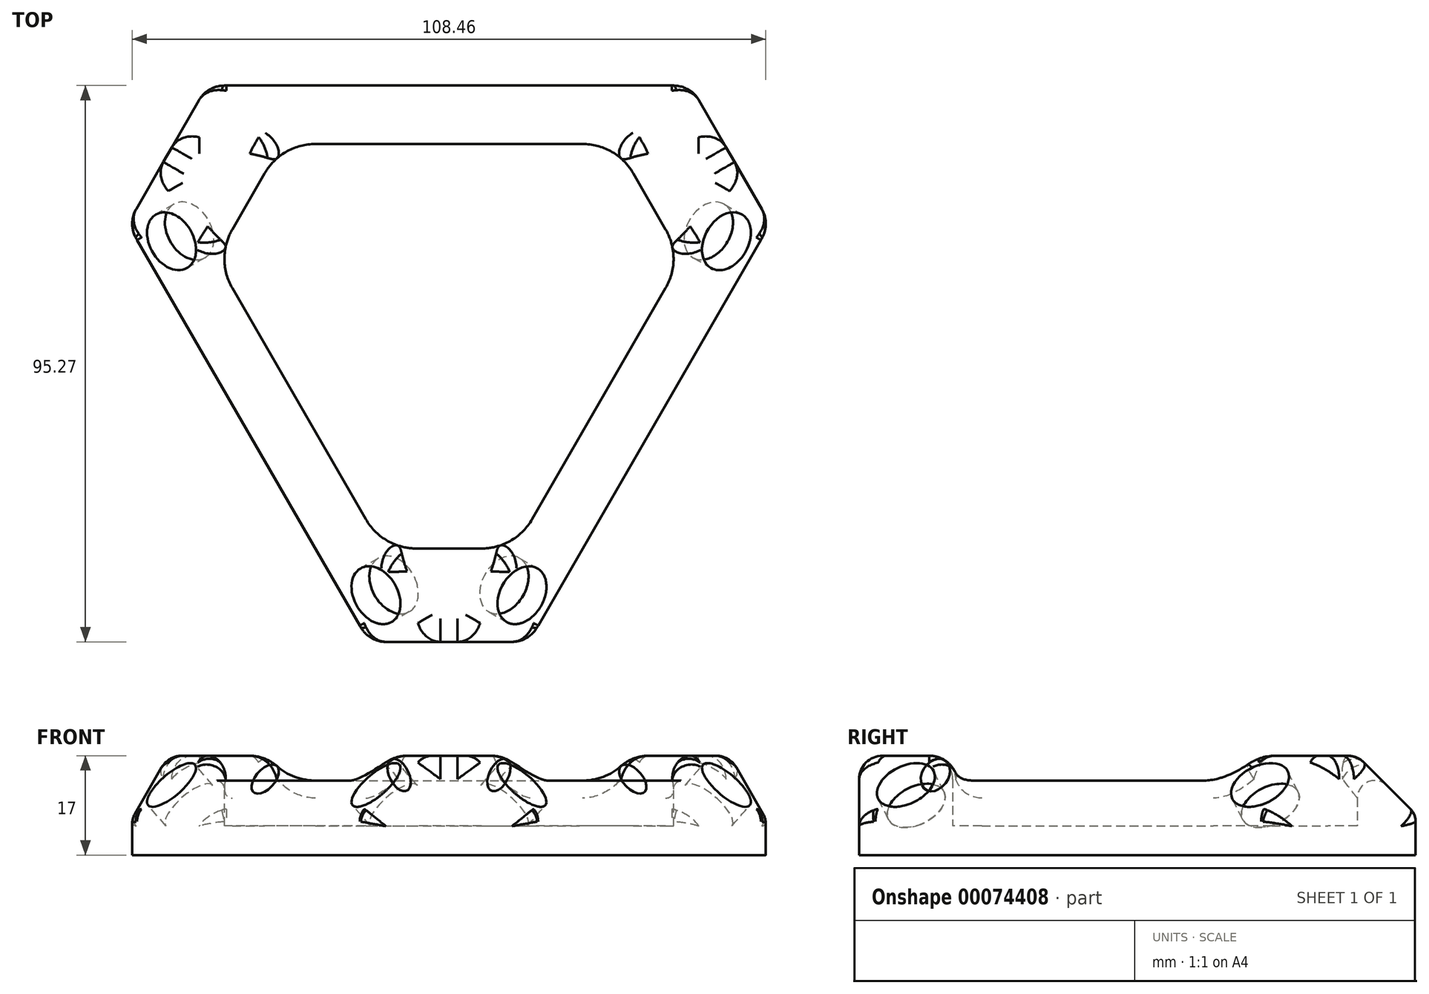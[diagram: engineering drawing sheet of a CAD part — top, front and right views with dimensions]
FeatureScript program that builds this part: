
annotation { "Feature Type Name" : "Feature", "Feature Type Description" : "" }
export const myFeature = defineFeature(function(context is Context, id is Id, definition is map)
    precondition{}
    {
        {
            var Q0;
            Q0=qCreatedBy(makeId("Top.planeOp"),FACE);
            var sketch = newSketch(context, id + "F0", { "sketchPlane" : qUnion([Q0])});
            skCircle(sketch, "E0.cCircle", {"center": v(0, 0) * mm, "radius": 34.64 * mm, "construction": true});
            skLineSegment(sketch, "E0.0", {"start": v(-60, 34.64) * mm, "end": v(60, 34.64) * mm, "construction": true});
            skLineSegment(sketch, "E0.1", {"start": v(60, 34.64) * mm, "end": v(0, -69.28) * mm, "construction": true});
            skLineSegment(sketch, "E0.2", {"start": v(0, -69.28) * mm, "end": v(-60, 34.64) * mm, "construction": true});
            skPoint(sketch, "E0.0.midPoint", {"position": v(0, 34.64) * mm});
            skCircle(sketch, "E1.cCircle", {"center": v(0, 0) * mm, "radius": 60.62 * mm, "construction": true});
            skLineSegment(sketch, "E1.0", {"start": v(-35, 60.62) * mm, "end": v(35, 60.62) * mm, "construction": true});
            skLineSegment(sketch, "E1.1", {"start": v(35, 60.62) * mm, "end": v(70, 0) * mm, "construction": true});
            skLineSegment(sketch, "E1.2", {"start": v(70, 0) * mm, "end": v(35, -60.62) * mm, "construction": true});
            skLineSegment(sketch, "E1.3", {"start": v(35, -60.62) * mm, "end": v(-35, -60.62) * mm, "construction": true});
            skLineSegment(sketch, "E1.4", {"start": v(-35, -60.62) * mm, "end": v(-70, 0) * mm, "construction": true});
            skLineSegment(sketch, "E1.5", {"start": v(-70, 0) * mm, "end": v(-35, 60.62) * mm, "construction": true});
            skPoint(sketch, "E1.0.midPoint", {"position": v(0, 60.62) * mm});
            skLineSegment(sketch, "E2", {"start": v(-35, 60.62) * mm, "end": v(-35, -60.62) * mm, "construction": true});
            skLineSegment(sketch, "E3", {"start": v(35, 60.62) * mm, "end": v(35, -60.62) * mm, "construction": true});
            skLineSegment(sketch, "E4", {"start": v(-70, 0) * mm, "end": v(35, 60.62) * mm, "construction": true});
            skLineSegment(sketch, "E5", {"start": v(-35, -60.62) * mm, "end": v(70, 0) * mm, "construction": true});
            skLineSegment(sketch, "E6", {"start": v(70, 0) * mm, "end": v(-35, 60.62) * mm, "construction": true});
            skLineSegment(sketch, "E7", {"start": v(35, -60.62) * mm, "end": v(-70, 0) * mm, "construction": true});
            skLineSegment(sketch, "E8", {"start": v(-35, 34.64) * mm, "end": v(35, 34.64) * mm, "construction": true});
            skLineSegment(sketch, "E9", {"start": v(35, 34.64) * mm, "end": v(47.5, 13) * mm, "construction": true});
            skLineSegment(sketch, "E10", {"start": v(-35, 34.64) * mm, "end": v(-47.5, 13) * mm, "construction": true});
            skLineSegment(sketch, "E11", {"start": v(-47.5, 13) * mm, "end": v(-12.5, -47.63) * mm, "construction": true});
            skLineSegment(sketch, "E12", {"start": v(-12.5, -47.63) * mm, "end": v(12.5, -47.63) * mm, "construction": true});
            skLineSegment(sketch, "E13", {"start": v(12.5, -47.63) * mm, "end": v(47.5, 13) * mm, "construction": true});
            skLineSegment(sketch, "E14", {"start": v(-28.65, 29.64) * mm, "end": v(28.65, 29.64) * mm});
            skLineSegment(sketch, "E15", {"start": v(28.65, 29.64) * mm, "end": v(40, 10) * mm});
            skLineSegment(sketch, "E16", {"start": v(40, 10) * mm, "end": v(11.35, -39.63) * mm});
            skLineSegment(sketch, "E17", {"start": v(11.35, -39.63) * mm, "end": v(-11.35, -39.63) * mm});
            skLineSegment(sketch, "E18", {"start": v(-11.35, -39.63) * mm, "end": v(-40, 10) * mm});
            skLineSegment(sketch, "E19", {"start": v(-40, 10) * mm, "end": v(-28.65, 29.64) * mm});
            skLineSegment(sketch, "E20", {"start": v(-41.35, 39.64) * mm, "end": v(41.35, 39.64) * mm});
            skLineSegment(sketch, "E21", {"start": v(41.35, 39.64) * mm, "end": v(55, 16) * mm});
            skLineSegment(sketch, "E22", {"start": v(55, 16) * mm, "end": v(13.65, -55.63) * mm});
            skLineSegment(sketch, "E23", {"start": v(13.65, -55.63) * mm, "end": v(-13.65, -55.63) * mm});
            skLineSegment(sketch, "E24", {"start": v(-13.65, -55.63) * mm, "end": v(-55, 16) * mm});
            skLineSegment(sketch, "E25", {"start": v(-55, 16) * mm, "end": v(-41.35, 39.64) * mm});
            skSolve(sketch);
        }
        {
            var Q0;
            Q0=makeQuery(id+"F0.imprint","IMPRINT",FACE,{"disambiguationData":[TD([[makeQuery(id+"F0.imprint","IMPRINT",EDGE,{"derivedFrom":sQuery(id+"F0.wireOp",EDGE,"E14")}),-1.0]])]});
            extrude(context, id + "F1", {"entities" : qUnion([Q0]), "depth" : 5 * mm});
        }
        {
            var Q0;
            Q0 = qSketchRegion(id + "F0", true);
            extrude(context, id + "F2", {"entities" : qUnion([Q0]), "operationType" : NewBodyOperationType.ADD, "depth" : 17 * mm});
        }
        {
            var Q0;
            Q0=makeQuery(id+"F2.opExtrude","CAP_EDGE",EDGE,{"disambiguationData":[OSD([sQuery(id+"F0.wireOp",EDGE,"E24")])],"isStart":false});
            var Q1;
            Q1=makeQuery(id+"F2.opExtrude","CAP_EDGE",EDGE,{"disambiguationData":[OSD([sQuery(id+"F0.wireOp",EDGE,"E22")])],"isStart":false});
            var Q2;
            Q2=makeQuery(id+"F2.opExtrude","CAP_EDGE",EDGE,{"disambiguationData":[OSD([sQuery(id+"F0.wireOp",EDGE,"E20")])],"isStart":false});
            chamfer(context, id + "F3", {"entities" : qUnion([Q0, Q1, Q2]), "width" : 10 * mm, "tangentPropagation" : true});
        }
        {
            var Q0;
            Q0=makeQuery(id+"F3.opChamfer","BLEND_FACE",FACE,{"disambiguationData":[OSD([sQuery(id+"F0.wireOp",EDGE,"E24")])]});
            var sketch = newSketch(context, id + "F4", { "sketchPlane" : qUnion([Q0])});
            skLineSegment(sketch, "E26", {"start": v(-40.38, 24.14) * mm, "end": v(15.58, -44.4) * mm, "construction": true});
            skLineSegment(sketch, "E27", {"start": v(-12.4, -10.13) * mm, "end": v(9.73, -37.24) * mm, "construction": true});
            skLineSegment(sketch, "E28", {"start": v(-12.4, -10.13) * mm, "end": v(-34.54, 16.99) * mm, "construction": true});
            skCircle(sketch, "E29", {"center": v(-34.54, 16.99) * mm, "radius": 5.3 * mm});
            skCircle(sketch, "E30", {"center": v(9.73, -37.24) * mm, "radius": 5.3 * mm});
            skSolve(sketch);
        }
        {
            var Q0;
            Q0=makeQuery(id+"F4.imprint","IMPRINT",FACE,{"disambiguationData":[TD([[makeQuery(id+"F4.imprint","IMPRINT",EDGE,{"derivedFrom":sQuery(id+"F4.wireOp",EDGE,"E29")}),1.0]])]});
            var Q1;
            Q1=makeQuery(id+"F4.imprint","IMPRINT",FACE,{"disambiguationData":[TD([[makeQuery(id+"F4.imprint","IMPRINT",EDGE,{"derivedFrom":sQuery(id+"F4.wireOp",EDGE,"E30")}),1.0]])]});
            extrude(context, id + "F5", {"entities" : qUnion([Q0, Q1]), "operationType" : NewBodyOperationType.REMOVE, "oppositeDirection" : true, "depth" : 5 * mm});
        }
        {
            var Q0;
            Q0=makeQuery(id+"F3.opChamfer","BLEND_FACE",FACE,{"disambiguationData":[OSD([sQuery(id+"F0.wireOp",EDGE,"E20")])]});
            var sketch = newSketch(context, id + "F6", { "sketchPlane" : qUnion([Q0])});
            skLineSegment(sketch, "E31", {"start": v(44.24, 16) * mm, "end": v(-44.24, 16) * mm, "construction": true});
            skLineSegment(sketch, "E32", {"start": v(0, 16) * mm, "end": v(-35, 16) * mm, "construction": true});
            skLineSegment(sketch, "E33", {"start": v(0, 16) * mm, "end": v(35, 16) * mm, "construction": true});
            skCircle(sketch, "E34", {"center": v(35, 16) * mm, "radius": 5.3 * mm});
            skCircle(sketch, "E35", {"center": v(-35, 16) * mm, "radius": 5.3 * mm});
            skSolve(sketch);
        }
        {
            var Q0;
            Q0=makeQuery(id+"F6.imprint","IMPRINT",FACE,{"disambiguationData":[TD([[makeQuery(id+"F6.imprint","IMPRINT",EDGE,{"derivedFrom":sQuery(id+"F6.wireOp",EDGE,"E34")}),1.0]])]});
            var Q1;
            Q1=makeQuery(id+"F6.imprint","IMPRINT",FACE,{"disambiguationData":[TD([[makeQuery(id+"F6.imprint","IMPRINT",EDGE,{"derivedFrom":sQuery(id+"F6.wireOp",EDGE,"E35")}),1.0]])]});
            extrude(context, id + "F7", {"entities" : qUnion([Q0, Q1]), "operationType" : NewBodyOperationType.REMOVE, "oppositeDirection" : true, "depth" : 5 * mm});
        }
        {
            var Q0;
            Q0=makeQuery(id+"F3.opChamfer","BLEND_FACE",FACE,{"disambiguationData":[OSD([sQuery(id+"F0.wireOp",EDGE,"E22")])]});
            var sketch = newSketch(context, id + "F8", { "sketchPlane" : qUnion([Q0])});
            skLineSegment(sketch, "E36", {"start": v(-15.58, -44.4) * mm, "end": v(40.38, 24.14) * mm, "construction": true});
            skLineSegment(sketch, "E37", {"start": v(12.4, -10.13) * mm, "end": v(34.54, 16.99) * mm, "construction": true});
            skLineSegment(sketch, "E38", {"start": v(12.4, -10.13) * mm, "end": v(-9.73, -37.24) * mm, "construction": true});
            skCircle(sketch, "E39", {"center": v(-9.73, -37.24) * mm, "radius": 5.3 * mm});
            skCircle(sketch, "E40", {"center": v(34.54, 16.99) * mm, "radius": 5.3 * mm});
            skSolve(sketch);
        }
        {
            var Q0;
            Q0=makeQuery(id+"F8.imprint","IMPRINT",FACE,{"disambiguationData":[TD([[makeQuery(id+"F8.imprint","IMPRINT",EDGE,{"derivedFrom":sQuery(id+"F8.wireOp",EDGE,"E39")}),1.0]])]});
            var Q1;
            Q1=makeQuery(id+"F8.imprint","IMPRINT",FACE,{"disambiguationData":[TD([[makeQuery(id+"F8.imprint","IMPRINT",EDGE,{"derivedFrom":sQuery(id+"F8.wireOp",EDGE,"E40")}),1.0]])]});
            extrude(context, id + "F9", {"entities" : qUnion([Q0, Q1]), "operationType" : NewBodyOperationType.REMOVE, "oppositeDirection" : true, "depth" : 5 * mm});
        }
        {
            var Q0;
            Q0=makeQuery(id+"F2.opExtrude","SWEPT_EDGE",EDGE,{"disambiguationData":[OSD([sQuery(id+"F0.wireOp",EDGE,"E16"),sQuery(id+"F0.wireOp",EDGE,"E17")])]});
            var Q1;
            Q1=makeQuery(id+"F2.opExtrude","SWEPT_EDGE",EDGE,{"disambiguationData":[OSD([sQuery(id+"F0.wireOp",EDGE,"E17"),sQuery(id+"F0.wireOp",EDGE,"E18")])]});
            var Q2;
            Q2=makeQuery(id+"F2.opExtrude","SWEPT_EDGE",EDGE,{"disambiguationData":[OSD([sQuery(id+"F0.wireOp",EDGE,"E14"),sQuery(id+"F0.wireOp",EDGE,"E15")])]});
            var Q3;
            Q3=makeQuery(id+"F2.opExtrude","SWEPT_EDGE",EDGE,{"disambiguationData":[OSD([sQuery(id+"F0.wireOp",EDGE,"E15"),sQuery(id+"F0.wireOp",EDGE,"E16")])]});
            var Q4;
            Q4=makeQuery(id+"F2.opExtrude","SWEPT_EDGE",EDGE,{"disambiguationData":[OSD([sQuery(id+"F0.wireOp",EDGE,"E18"),sQuery(id+"F0.wireOp",EDGE,"E19")])]});
            var Q5;
            Q5=makeQuery(id+"F2.opExtrude","SWEPT_EDGE",EDGE,{"disambiguationData":[OSD([sQuery(id+"F0.wireOp",EDGE,"E14"),sQuery(id+"F0.wireOp",EDGE,"E19")])]});
            fillet(context, id + "F10", {"entities" : qUnion([Q0, Q1, Q2, Q3, Q4, Q5]), "radius" : 10 * mm, "tangentPropagation" : true, "allowEdgeOverflow" : false});
        }
        {
            var Q0;
            Q0=makeQuery(id+"F3.opChamfer","BLEND_EDGE",EDGE,{"blendedFrom":[makeQuery(id+"F2.opExtrude","CAP_EDGE",EDGE,{"disambiguationData":[OSD([sQuery(id+"F0.wireOp",EDGE,"E24")])],"isStart":false}),makeQuery(id+"F2.opExtrude","SWEPT_FACE",FACE,{"disambiguationData":[OSD([sQuery(id+"F0.wireOp",EDGE,"E23")])]})],"blendedInto":[makeQuery(id+"F2.opExtrude","SWEPT_FACE",FACE,{"disambiguationData":[OSD([sQuery(id+"F0.wireOp",EDGE,"E23")])]})]});
            var Q1;
            Q1=makeQuery(id+"F3.opChamfer","BLEND_EDGE",EDGE,{"blendedFrom":[makeQuery(id+"F2.opExtrude","CAP_EDGE",EDGE,{"disambiguationData":[OSD([sQuery(id+"F0.wireOp",EDGE,"E22")])],"isStart":false}),makeQuery(id+"F2.opExtrude","SWEPT_FACE",FACE,{"disambiguationData":[OSD([sQuery(id+"F0.wireOp",EDGE,"E23")])]})],"blendedInto":[makeQuery(id+"F2.opExtrude","SWEPT_FACE",FACE,{"disambiguationData":[OSD([sQuery(id+"F0.wireOp",EDGE,"E23")])]})]});
            var Q2;
            Q2=makeQuery(id+"F2.opExtrude","SWEPT_EDGE",EDGE,{"disambiguationData":[OSD([sQuery(id+"F0.wireOp",EDGE,"E22"),sQuery(id+"F0.wireOp",EDGE,"E23")])]});
            var Q3;
            Q3=makeQuery(id+"F2.opExtrude","SWEPT_EDGE",EDGE,{"disambiguationData":[OSD([sQuery(id+"F0.wireOp",EDGE,"E23"),sQuery(id+"F0.wireOp",EDGE,"E24")])]});
            var Q4;
            Q4=makeQuery(id+"F2.opExtrude","SWEPT_EDGE",EDGE,{"disambiguationData":[OSD([sQuery(id+"F0.wireOp",EDGE,"E21"),sQuery(id+"F0.wireOp",EDGE,"E22")])]});
            var Q5;
            Q5=makeQuery(id+"F3.opChamfer","BLEND_EDGE",EDGE,{"blendedFrom":[makeQuery(id+"F2.opExtrude","CAP_EDGE",EDGE,{"disambiguationData":[OSD([sQuery(id+"F0.wireOp",EDGE,"E22")])],"isStart":false}),makeQuery(id+"F2.opExtrude","SWEPT_FACE",FACE,{"disambiguationData":[OSD([sQuery(id+"F0.wireOp",EDGE,"E21")])]})],"blendedInto":[makeQuery(id+"F2.opExtrude","SWEPT_FACE",FACE,{"disambiguationData":[OSD([sQuery(id+"F0.wireOp",EDGE,"E21")])]})]});
            var Q6;
            Q6=makeQuery(id+"F3.opChamfer","BLEND_EDGE",EDGE,{"blendedFrom":[makeQuery(id+"F2.opExtrude","CAP_EDGE",EDGE,{"disambiguationData":[OSD([sQuery(id+"F0.wireOp",EDGE,"E20")])],"isStart":false}),makeQuery(id+"F2.opExtrude","SWEPT_FACE",FACE,{"disambiguationData":[OSD([sQuery(id+"F0.wireOp",EDGE,"E21")])]})],"blendedInto":[makeQuery(id+"F2.opExtrude","SWEPT_FACE",FACE,{"disambiguationData":[OSD([sQuery(id+"F0.wireOp",EDGE,"E21")])]})]});
            var Q7;
            Q7=makeQuery(id+"F2.opExtrude","SWEPT_EDGE",EDGE,{"disambiguationData":[OSD([sQuery(id+"F0.wireOp",EDGE,"E20"),sQuery(id+"F0.wireOp",EDGE,"E21")])]});
            var Q8;
            Q8=makeQuery(id+"F2.opExtrude","SWEPT_EDGE",EDGE,{"disambiguationData":[OSD([sQuery(id+"F0.wireOp",EDGE,"E24"),sQuery(id+"F0.wireOp",EDGE,"E25")])]});
            var Q9;
            Q9=makeQuery(id+"F3.opChamfer","BLEND_EDGE",EDGE,{"blendedFrom":[makeQuery(id+"F2.opExtrude","CAP_EDGE",EDGE,{"disambiguationData":[OSD([sQuery(id+"F0.wireOp",EDGE,"E24")])],"isStart":false}),makeQuery(id+"F2.opExtrude","SWEPT_FACE",FACE,{"disambiguationData":[OSD([sQuery(id+"F0.wireOp",EDGE,"E25")])]})],"blendedInto":[makeQuery(id+"F2.opExtrude","SWEPT_FACE",FACE,{"disambiguationData":[OSD([sQuery(id+"F0.wireOp",EDGE,"E25")])]})]});
            var Q10;
            Q10=makeQuery(id+"F3.opChamfer","BLEND_EDGE",EDGE,{"blendedFrom":[makeQuery(id+"F2.opExtrude","CAP_EDGE",EDGE,{"disambiguationData":[OSD([sQuery(id+"F0.wireOp",EDGE,"E20")])],"isStart":false}),makeQuery(id+"F2.opExtrude","SWEPT_FACE",FACE,{"disambiguationData":[OSD([sQuery(id+"F0.wireOp",EDGE,"E25")])]})],"blendedInto":[makeQuery(id+"F2.opExtrude","SWEPT_FACE",FACE,{"disambiguationData":[OSD([sQuery(id+"F0.wireOp",EDGE,"E25")])]})]});
            var Q11;
            Q11=makeQuery(id+"F2.opExtrude","SWEPT_EDGE",EDGE,{"disambiguationData":[OSD([sQuery(id+"F0.wireOp",EDGE,"E20"),sQuery(id+"F0.wireOp",EDGE,"E25")])]});
            fillet(context, id + "F11", {"entities" : qUnion([Q0, Q1, Q2, Q3, Q4, Q5, Q6, Q7, Q8, Q9, Q10, Q11]), "radius" : 5 * mm, "tangentPropagation" : true, "allowEdgeOverflow" : false});
        }
        {
            var Q0;
            Q0=makeQuery(id+"F3.opChamfer","BLEND_EDGE",EDGE,{"blendedFrom":[makeQuery(id+"F2.opExtrude","CAP_EDGE",EDGE,{"disambiguationData":[OSD([sQuery(id+"F0.wireOp",EDGE,"E20")])],"isStart":false}),makeQuery(id+"F2.opExtrude","SWEPT_FACE",FACE,{"disambiguationData":[OSD([sQuery(id+"F0.wireOp",EDGE,"E14")])]})],"blendedInto":[makeQuery(id+"F2.opExtrude","SWEPT_FACE",FACE,{"disambiguationData":[OSD([sQuery(id+"F0.wireOp",EDGE,"E14")])]})]});
            var Q1;
            Q1=makeQuery(id+"F3.opChamfer","BLEND_EDGE",EDGE,{"blendedFrom":[makeQuery(id+"F2.opExtrude","CAP_EDGE",EDGE,{"disambiguationData":[OSD([sQuery(id+"F0.wireOp",EDGE,"E22")])],"isStart":false}),makeQuery(id+"F2.opExtrude","SWEPT_FACE",FACE,{"disambiguationData":[OSD([sQuery(id+"F0.wireOp",EDGE,"E16")])]})],"blendedInto":[makeQuery(id+"F2.opExtrude","SWEPT_FACE",FACE,{"disambiguationData":[OSD([sQuery(id+"F0.wireOp",EDGE,"E16")])]})]});
            var Q2;
            Q2=makeQuery(id+"F3.opChamfer","BLEND_EDGE",EDGE,{"blendedFrom":[makeQuery(id+"F2.opExtrude","CAP_EDGE",EDGE,{"disambiguationData":[OSD([sQuery(id+"F0.wireOp",EDGE,"E24")])],"isStart":false}),makeQuery(id+"F2.opExtrude","SWEPT_FACE",FACE,{"disambiguationData":[OSD([sQuery(id+"F0.wireOp",EDGE,"E18")])]})],"blendedInto":[makeQuery(id+"F2.opExtrude","SWEPT_FACE",FACE,{"disambiguationData":[OSD([sQuery(id+"F0.wireOp",EDGE,"E18")])]})]});
            var Q3;
            {var subQ0=sQuery(id+"F0.wireOp",EDGE,"E20");Q3=makeQuery(id+"F3.opChamfer","BLEND_EDGE",EDGE,{"blendedFrom":[makeQuery(id+"F2.opExtrude","CAP_EDGE",EDGE,{"disambiguationData":[OSD([subQ0])],"isStart":false}),makeQuery(id+"F2.opExtrude","SWEPT_FACE",FACE,{"disambiguationData":[OSD([subQ0])]})],"blendedInto":[makeQuery(id+"F2.opExtrude","SWEPT_FACE",FACE,{"disambiguationData":[OSD([subQ0])]})]});}
            var Q4;
            {var subQ0=sQuery(id+"F0.wireOp",EDGE,"E24");Q4=makeQuery(id+"F3.opChamfer","BLEND_EDGE",EDGE,{"blendedFrom":[makeQuery(id+"F2.opExtrude","CAP_EDGE",EDGE,{"disambiguationData":[OSD([subQ0])],"isStart":false}),makeQuery(id+"F2.opExtrude","SWEPT_FACE",FACE,{"disambiguationData":[OSD([subQ0])]})],"blendedInto":[makeQuery(id+"F2.opExtrude","SWEPT_FACE",FACE,{"disambiguationData":[OSD([subQ0])]})]});}
            var Q5;
            {var subQ0=sQuery(id+"F0.wireOp",EDGE,"E22");Q5=makeQuery(id+"F3.opChamfer","BLEND_EDGE",EDGE,{"blendedFrom":[makeQuery(id+"F2.opExtrude","CAP_EDGE",EDGE,{"disambiguationData":[OSD([subQ0])],"isStart":false}),makeQuery(id+"F2.opExtrude","SWEPT_FACE",FACE,{"disambiguationData":[OSD([subQ0])]})],"blendedInto":[makeQuery(id+"F2.opExtrude","SWEPT_FACE",FACE,{"disambiguationData":[OSD([subQ0])]})]});}
            fillet(context, id + "F12", {"entities" : qUnion([Q0, Q1, Q2, Q3, Q4, Q5]), "radius" : 3 * mm, "tangentPropagation" : true, "allowEdgeOverflow" : false});
        }
        {
            var Q0;
            Q0=makeQuery(id+"F2.opExtrude","CAP_EDGE",EDGE,{"disambiguationData":[OSD([sQuery(id+"F0.wireOp",EDGE,"E19")])],"isStart":false});
            var Q1;
            {var subQ0=sQuery(id+"F0.wireOp",EDGE,"E24");Q1=makeQuery(id+"F3.opChamfer","BLEND_EDGE",EDGE,{"disambiguationData":[OD(1.0)],"blendedFrom":[makeQuery(id+"F2.opExtrude","CAP_EDGE",EDGE,{"disambiguationData":[OSD([subQ0])],"isStart":false}),makeQuery(id+"F2.opExtrude","CAP_FACE",FACE,{"disambiguationData":[OSD([sQuery(id+"F0.wireOp",EDGE,"E14"),sQuery(id+"F0.wireOp",EDGE,"E15"),sQuery(id+"F0.wireOp",EDGE,"E16"),sQuery(id+"F0.wireOp",EDGE,"E17"),sQuery(id+"F0.wireOp",EDGE,"E18"),sQuery(id+"F0.wireOp",EDGE,"E19"),sQuery(id+"F0.wireOp",EDGE,"E20"),sQuery(id+"F0.wireOp",EDGE,"E21"),sQuery(id+"F0.wireOp",EDGE,"E22"),sQuery(id+"F0.wireOp",EDGE,"E23"),subQ0,sQuery(id+"F0.wireOp",EDGE,"E25")])],"isStart":false})],"blendedInto":[makeQuery(id+"F2.opExtrude","CAP_FACE",FACE,{"disambiguationData":[OSD([sQuery(id+"F0.wireOp",EDGE,"E14"),sQuery(id+"F0.wireOp",EDGE,"E15"),sQuery(id+"F0.wireOp",EDGE,"E16"),sQuery(id+"F0.wireOp",EDGE,"E17"),sQuery(id+"F0.wireOp",EDGE,"E18"),sQuery(id+"F0.wireOp",EDGE,"E19"),sQuery(id+"F0.wireOp",EDGE,"E20"),sQuery(id+"F0.wireOp",EDGE,"E21"),sQuery(id+"F0.wireOp",EDGE,"E22"),sQuery(id+"F0.wireOp",EDGE,"E23"),subQ0,sQuery(id+"F0.wireOp",EDGE,"E25")])],"isStart":false})]});}
            var Q2;
            {var subQ0=sQuery(id+"F0.wireOp",EDGE,"E20");Q2=makeQuery(id+"F3.opChamfer","BLEND_EDGE",EDGE,{"disambiguationData":[OD(1.0)],"blendedFrom":[makeQuery(id+"F2.opExtrude","CAP_EDGE",EDGE,{"disambiguationData":[OSD([subQ0])],"isStart":false}),makeQuery(id+"F2.opExtrude","CAP_FACE",FACE,{"disambiguationData":[OSD([sQuery(id+"F0.wireOp",EDGE,"E14"),sQuery(id+"F0.wireOp",EDGE,"E15"),sQuery(id+"F0.wireOp",EDGE,"E16"),sQuery(id+"F0.wireOp",EDGE,"E17"),sQuery(id+"F0.wireOp",EDGE,"E18"),sQuery(id+"F0.wireOp",EDGE,"E19"),subQ0,sQuery(id+"F0.wireOp",EDGE,"E21"),sQuery(id+"F0.wireOp",EDGE,"E22"),sQuery(id+"F0.wireOp",EDGE,"E23"),sQuery(id+"F0.wireOp",EDGE,"E24"),sQuery(id+"F0.wireOp",EDGE,"E25")])],"isStart":false})],"blendedInto":[makeQuery(id+"F2.opExtrude","CAP_FACE",FACE,{"disambiguationData":[OSD([sQuery(id+"F0.wireOp",EDGE,"E14"),sQuery(id+"F0.wireOp",EDGE,"E15"),sQuery(id+"F0.wireOp",EDGE,"E16"),sQuery(id+"F0.wireOp",EDGE,"E17"),sQuery(id+"F0.wireOp",EDGE,"E18"),sQuery(id+"F0.wireOp",EDGE,"E19"),subQ0,sQuery(id+"F0.wireOp",EDGE,"E21"),sQuery(id+"F0.wireOp",EDGE,"E22"),sQuery(id+"F0.wireOp",EDGE,"E23"),sQuery(id+"F0.wireOp",EDGE,"E24"),sQuery(id+"F0.wireOp",EDGE,"E25")])],"isStart":false})]});}
            var Q3;
            {var subQ0=sQuery(id+"F0.wireOp",EDGE,"E22");Q3=makeQuery(id+"F3.opChamfer","BLEND_EDGE",EDGE,{"disambiguationData":[OD(1.0)],"blendedFrom":[makeQuery(id+"F2.opExtrude","CAP_EDGE",EDGE,{"disambiguationData":[OSD([subQ0])],"isStart":false}),makeQuery(id+"F2.opExtrude","CAP_FACE",FACE,{"disambiguationData":[OSD([sQuery(id+"F0.wireOp",EDGE,"E14"),sQuery(id+"F0.wireOp",EDGE,"E15"),sQuery(id+"F0.wireOp",EDGE,"E16"),sQuery(id+"F0.wireOp",EDGE,"E17"),sQuery(id+"F0.wireOp",EDGE,"E18"),sQuery(id+"F0.wireOp",EDGE,"E19"),sQuery(id+"F0.wireOp",EDGE,"E20"),sQuery(id+"F0.wireOp",EDGE,"E21"),subQ0,sQuery(id+"F0.wireOp",EDGE,"E23"),sQuery(id+"F0.wireOp",EDGE,"E24"),sQuery(id+"F0.wireOp",EDGE,"E25")])],"isStart":false})],"blendedInto":[makeQuery(id+"F2.opExtrude","CAP_FACE",FACE,{"disambiguationData":[OSD([sQuery(id+"F0.wireOp",EDGE,"E14"),sQuery(id+"F0.wireOp",EDGE,"E15"),sQuery(id+"F0.wireOp",EDGE,"E16"),sQuery(id+"F0.wireOp",EDGE,"E17"),sQuery(id+"F0.wireOp",EDGE,"E18"),sQuery(id+"F0.wireOp",EDGE,"E19"),sQuery(id+"F0.wireOp",EDGE,"E20"),sQuery(id+"F0.wireOp",EDGE,"E21"),subQ0,sQuery(id+"F0.wireOp",EDGE,"E23"),sQuery(id+"F0.wireOp",EDGE,"E24"),sQuery(id+"F0.wireOp",EDGE,"E25")])],"isStart":false})]});}
            var Q4;
            Q4=makeQuery(id+"F2.opExtrude","CAP_EDGE",EDGE,{"disambiguationData":[OSD([sQuery(id+"F0.wireOp",EDGE,"E17")])],"isStart":false});
            var Q5;
            {var subQ0=sQuery(id+"F0.wireOp",EDGE,"E24");Q5=makeQuery(id+"F3.opChamfer","BLEND_EDGE",EDGE,{"disambiguationData":[OD(0.0)],"blendedFrom":[makeQuery(id+"F2.opExtrude","CAP_EDGE",EDGE,{"disambiguationData":[OSD([subQ0])],"isStart":false}),makeQuery(id+"F2.opExtrude","CAP_FACE",FACE,{"disambiguationData":[OSD([sQuery(id+"F0.wireOp",EDGE,"E14"),sQuery(id+"F0.wireOp",EDGE,"E15"),sQuery(id+"F0.wireOp",EDGE,"E16"),sQuery(id+"F0.wireOp",EDGE,"E17"),sQuery(id+"F0.wireOp",EDGE,"E18"),sQuery(id+"F0.wireOp",EDGE,"E19"),sQuery(id+"F0.wireOp",EDGE,"E20"),sQuery(id+"F0.wireOp",EDGE,"E21"),sQuery(id+"F0.wireOp",EDGE,"E22"),sQuery(id+"F0.wireOp",EDGE,"E23"),subQ0,sQuery(id+"F0.wireOp",EDGE,"E25")])],"isStart":false})],"blendedInto":[makeQuery(id+"F2.opExtrude","CAP_FACE",FACE,{"disambiguationData":[OSD([sQuery(id+"F0.wireOp",EDGE,"E14"),sQuery(id+"F0.wireOp",EDGE,"E15"),sQuery(id+"F0.wireOp",EDGE,"E16"),sQuery(id+"F0.wireOp",EDGE,"E17"),sQuery(id+"F0.wireOp",EDGE,"E18"),sQuery(id+"F0.wireOp",EDGE,"E19"),sQuery(id+"F0.wireOp",EDGE,"E20"),sQuery(id+"F0.wireOp",EDGE,"E21"),sQuery(id+"F0.wireOp",EDGE,"E22"),sQuery(id+"F0.wireOp",EDGE,"E23"),subQ0,sQuery(id+"F0.wireOp",EDGE,"E25")])],"isStart":false})]});}
            var Q6;
            {var subQ0=sQuery(id+"F0.wireOp",EDGE,"E22");Q6=makeQuery(id+"F3.opChamfer","BLEND_EDGE",EDGE,{"disambiguationData":[OD(0.0)],"blendedFrom":[makeQuery(id+"F2.opExtrude","CAP_EDGE",EDGE,{"disambiguationData":[OSD([subQ0])],"isStart":false}),makeQuery(id+"F2.opExtrude","CAP_FACE",FACE,{"disambiguationData":[OSD([sQuery(id+"F0.wireOp",EDGE,"E14"),sQuery(id+"F0.wireOp",EDGE,"E15"),sQuery(id+"F0.wireOp",EDGE,"E16"),sQuery(id+"F0.wireOp",EDGE,"E17"),sQuery(id+"F0.wireOp",EDGE,"E18"),sQuery(id+"F0.wireOp",EDGE,"E19"),sQuery(id+"F0.wireOp",EDGE,"E20"),sQuery(id+"F0.wireOp",EDGE,"E21"),subQ0,sQuery(id+"F0.wireOp",EDGE,"E23"),sQuery(id+"F0.wireOp",EDGE,"E24"),sQuery(id+"F0.wireOp",EDGE,"E25")])],"isStart":false})],"blendedInto":[makeQuery(id+"F2.opExtrude","CAP_FACE",FACE,{"disambiguationData":[OSD([sQuery(id+"F0.wireOp",EDGE,"E14"),sQuery(id+"F0.wireOp",EDGE,"E15"),sQuery(id+"F0.wireOp",EDGE,"E16"),sQuery(id+"F0.wireOp",EDGE,"E17"),sQuery(id+"F0.wireOp",EDGE,"E18"),sQuery(id+"F0.wireOp",EDGE,"E19"),sQuery(id+"F0.wireOp",EDGE,"E20"),sQuery(id+"F0.wireOp",EDGE,"E21"),subQ0,sQuery(id+"F0.wireOp",EDGE,"E23"),sQuery(id+"F0.wireOp",EDGE,"E24"),sQuery(id+"F0.wireOp",EDGE,"E25")])],"isStart":false})]});}
            var Q7;
            Q7=makeQuery(id+"F2.opExtrude","CAP_EDGE",EDGE,{"disambiguationData":[OSD([sQuery(id+"F0.wireOp",EDGE,"E15")])],"isStart":false});
            var Q8;
            {var subQ0=sQuery(id+"F0.wireOp",EDGE,"E20");Q8=makeQuery(id+"F3.opChamfer","BLEND_EDGE",EDGE,{"disambiguationData":[OD(0.0)],"blendedFrom":[makeQuery(id+"F2.opExtrude","CAP_EDGE",EDGE,{"disambiguationData":[OSD([subQ0])],"isStart":false}),makeQuery(id+"F2.opExtrude","CAP_FACE",FACE,{"disambiguationData":[OSD([sQuery(id+"F0.wireOp",EDGE,"E14"),sQuery(id+"F0.wireOp",EDGE,"E15"),sQuery(id+"F0.wireOp",EDGE,"E16"),sQuery(id+"F0.wireOp",EDGE,"E17"),sQuery(id+"F0.wireOp",EDGE,"E18"),sQuery(id+"F0.wireOp",EDGE,"E19"),subQ0,sQuery(id+"F0.wireOp",EDGE,"E21"),sQuery(id+"F0.wireOp",EDGE,"E22"),sQuery(id+"F0.wireOp",EDGE,"E23"),sQuery(id+"F0.wireOp",EDGE,"E24"),sQuery(id+"F0.wireOp",EDGE,"E25")])],"isStart":false})],"blendedInto":[makeQuery(id+"F2.opExtrude","CAP_FACE",FACE,{"disambiguationData":[OSD([sQuery(id+"F0.wireOp",EDGE,"E14"),sQuery(id+"F0.wireOp",EDGE,"E15"),sQuery(id+"F0.wireOp",EDGE,"E16"),sQuery(id+"F0.wireOp",EDGE,"E17"),sQuery(id+"F0.wireOp",EDGE,"E18"),sQuery(id+"F0.wireOp",EDGE,"E19"),subQ0,sQuery(id+"F0.wireOp",EDGE,"E21"),sQuery(id+"F0.wireOp",EDGE,"E22"),sQuery(id+"F0.wireOp",EDGE,"E23"),sQuery(id+"F0.wireOp",EDGE,"E24"),sQuery(id+"F0.wireOp",EDGE,"E25")])],"isStart":false})]});}
            fillet(context, id + "F13", {"entities" : qUnion([Q0, Q1, Q2, Q3, Q4, Q5, Q6, Q7, Q8]), "radius" : 4 * mm, "tangentPropagation" : true, "allowEdgeOverflow" : false});
        }
    });
